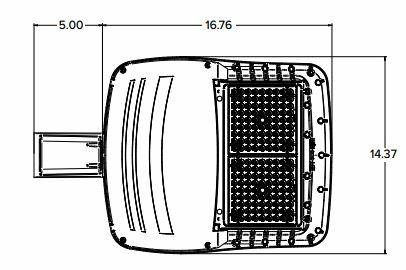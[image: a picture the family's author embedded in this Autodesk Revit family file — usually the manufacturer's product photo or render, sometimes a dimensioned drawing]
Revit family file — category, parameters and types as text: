
# Revit family: VP-3-A
name_source: partatom
category: Lighting Fixtures
units: mm (PartAtom-declared; Revit-internal decimal feet)

## family parameters
Cut with Voids When Loaded = No
Host = Face
Light Source = No
OmniClass Number = 23.80.70.11.14.17
OmniClass Title = Direct/Indirect
Part Type = Normal
Room Calculation Point = No
Round Connector Dimension = Use Diameter
Shared = Yes

## types (1)
- VP-3-A
    Apparent Load = 423 VA
    Assembly Code = D5020200
    Brand = Beacon
    CRI = 70
    Certification = UL
    Cool Grey = Cool Grey
    Default Elevation = 48 "
    Description = The Viper is an extremely versatile area/site luminaire which blends design, performance, and technology for a variety of applications.
    Features = Featuring two different optical technologies, Micro Strike and Strike Optics, which provide the best distribution patterns for retrofit or new construction
Vibration rated for high vibration applications including bridges and overpasses
Control options including photo control, occupancy sensing, NX Lighting Controls, wiSCAPE and 7-Pin with networked controls
Mounting options include: Arm, Universal Arm, Adjustable Arm, Mast Arm, Decorative Arm, Knuckle, Trunnion, Wall
Distribution options include: Auto Front Row, Type 2, Type 3, Type 4 Forward, Type 4 Wide, Type 5 Narrow, Type 5 Medium, Type 5 Wide, Type 5 Rectangular, Corner Optic, and Tennis Court
    Finish = Arctic White
    Glass = Glass
    Grey = Grey
    Lamp = LED
    Light Output = 30846 cd/m²
    Load Classification = Lighting
    Manufacturer = Current Lighting
    Matt Black = Matt Black
    Matt Grey = MATT GREY
    Matt White = Matt White
    Model = VP-3-A
    Name = Viper Area Size 3
    Power Factor = 0.9
    Product Documentation Link = https://cdn.currentlighting.com
    Product Page URL = https://www.currentlighting.com
    Type Comments = Lighting Fixture
    URL = https://www.currentlighting.com
    Voltage = 120 V
    Warranty = Five year warranty
    Wattage Comments = 423 W

## geometry (parser evidence)
native form markers: Blend x4, Sweep x5
no freeform markers — native parametric forms only
